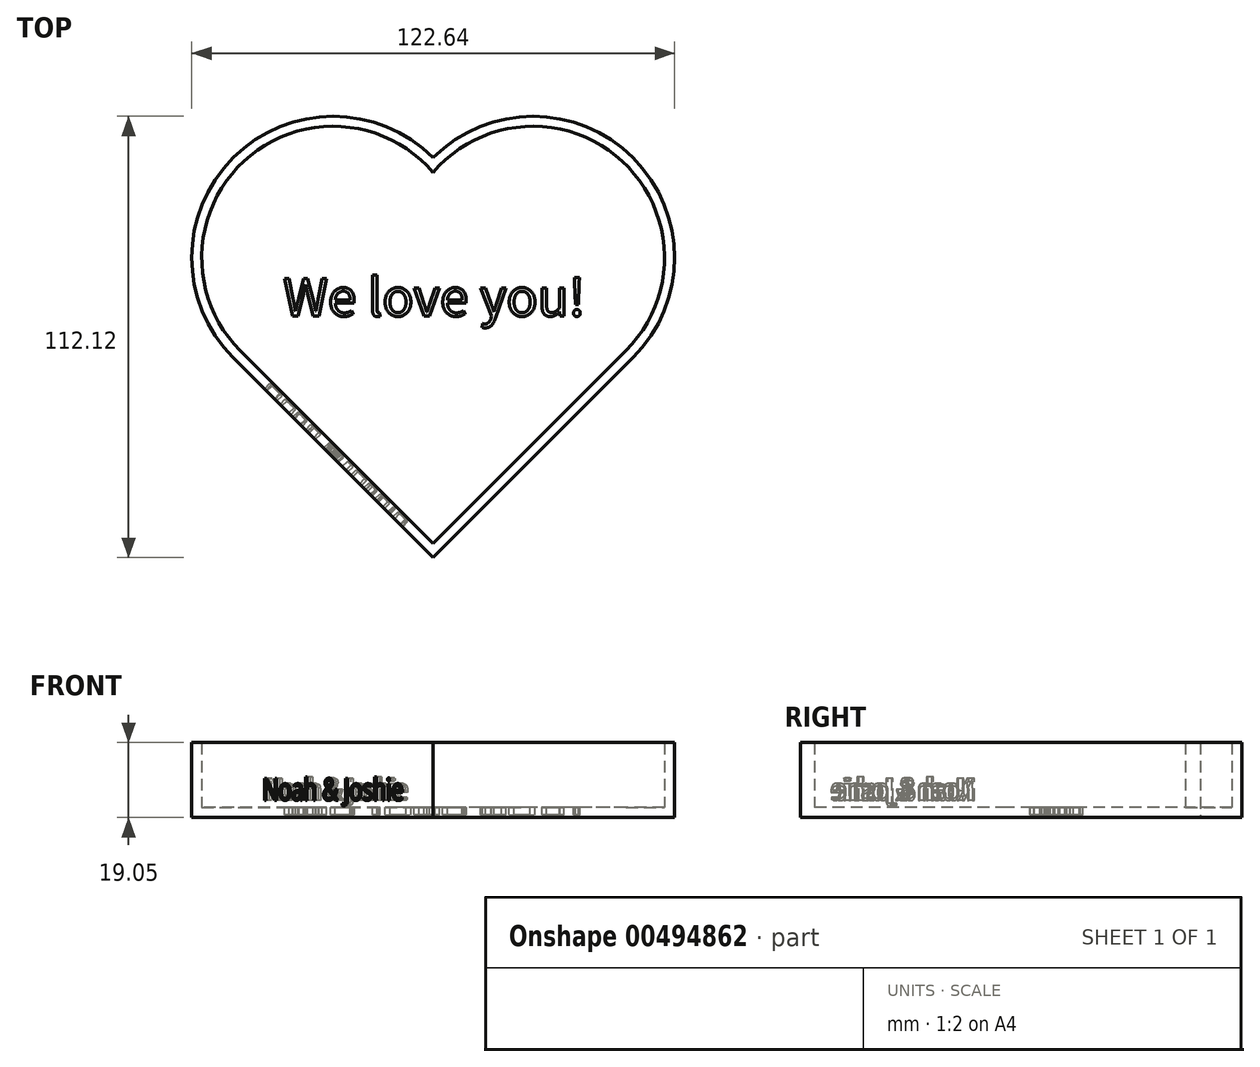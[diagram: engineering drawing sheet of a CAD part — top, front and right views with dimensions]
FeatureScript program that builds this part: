
annotation { "Feature Type Name" : "Feature", "Feature Type Description" : "" }
export const myFeature = defineFeature(function(context is Context, id is Id, definition is map)
    precondition{}
    {
        {
            var Q0;
            Q0=qCreatedBy(makeId("Top.planeOp"),FACE);
            var sketch = newSketch(context, id + "F0", { "sketchPlane" : qUnion([Q0])});
            skLineSegment(sketch, "E0", {"start": v(0, 50.8) * mm, "end": v(0, 0) * mm, "construction": true});
            skLineSegment(sketch, "E1", {"start": v(0, 0) * mm, "end": v(50.8, 0) * mm, "construction": true});
            skLineSegment(sketch, "E2", {"start": v(0, 0) * mm, "end": v(0, -50.8) * mm, "construction": true});
            skLineSegment(sketch, "E3", {"start": v(0, 0) * mm, "end": v(-50.8, 0) * mm, "construction": true});
            skLineSegment(sketch, "E4", {"start": v(-50.8, 0) * mm, "end": v(0, -50.8) * mm});
            skLineSegment(sketch, "E5", {"start": v(50.8, 0) * mm, "end": v(0, -50.8) * mm});
            skArc(sketch, "E6", {"start": v(0, 50.8) * mm, "mid": v(-50.8, 50.8) * mm, "end": v(-50.8, 0) * mm});
            skArc(sketch, "E7", {"start": v(50.8, 0) * mm, "mid": v(50.8, 50.8) * mm, "end": v(0, 50.8) * mm});
            skSolve(sketch);
        }
        {
            var Q0;
            Q0=makeQuery(id+"F0.imprint","IMPRINT",FACE,{"disambiguationData":[TD([[makeQuery(id+"F0.imprint","IMPRINT",EDGE,{"derivedFrom":sQuery(id+"F0.wireOp",EDGE,"E4")}),1.0]])]});
            extrude(context, id + "F1", {"entities" : qUnion([Q0]), "depth" : 19.05 * mm});
        }
        {
            var Q0;
            Q0=makeQuery(id+"F1.opExtrude","CAP_FACE",FACE,{"disambiguationData":[OSD([sQuery(id+"F0.wireOp",EDGE,"E4"),sQuery(id+"F0.wireOp",EDGE,"E5"),sQuery(id+"F0.wireOp",EDGE,"E6"),sQuery(id+"F0.wireOp",EDGE,"E7")])],"isStart":false});
            shell(context, id + "F2", {"entities" : qUnion([Q0]), "thickness" : 2.54 * mm});
        }
        {
            var Q0;
            Q0=makeQuery(id+"F2.opShell","OFFSET_FACE",FACE,{"disambiguationData":[OSD([sQuery(id+"F0.wireOp",EDGE,"E4"),sQuery(id+"F0.wireOp",EDGE,"E5"),sQuery(id+"F0.wireOp",EDGE,"E6"),sQuery(id+"F0.wireOp",EDGE,"E7")])]});
            var sketch = newSketch(context, id + "F3", { "sketchPlane" : qUnion([Q0])});
            skLineSegment(sketch, "E8.bottom", {"start": v(38.1, 19.96) * mm, "end": v(-38.1, 19.96) * mm, "construction": true});
            skLineSegment(sketch, "E8.top", {"start": v(38.1, 10.6) * mm, "end": v(-38.1, 10.6) * mm, "construction": true});
            skLineSegment(sketch, "E8.left", {"start": v(38.1, 19.96) * mm, "end": v(38.1, 10.6) * mm, "construction": true});
            skLineSegment(sketch, "E8.right", {"start": v(-38.1, 19.96) * mm, "end": v(-38.1, 10.6) * mm, "construction": true});
            skPoint(sketch, "E8.middle", {"position": v(0, 15.28) * mm});
            skText(sketch, "E9", { "text": "We love you!", "fontName": "NotoSansCJKkr-Regular.otf"});
            const initialGuessF3  = {"E9": [-0.0381, 0.0106, 1, 0, 0.00936]};
            skSetInitialGuess(sketch, initialGuessF3);
            skSolve(sketch);
        }
        {
            var Q0;
            Q0 = qSketchRegion(id + "F3", true);
            extrude(context, id + "F4", {"entities" : qUnion([Q0]), "operationType" : NewBodyOperationType.REMOVE, "oppositeDirection" : true, "depth" : 1.9 * mm});
        }
        {
            var Q0;
            Q0=makeQuery(id+"F1.opExtrude","SWEPT_FACE",FACE,{"disambiguationData":[OSD([sQuery(id+"F0.wireOp",EDGE,"E4")])]});
            var sketch = newSketch(context, id + "F5", { "sketchPlane" : qUnion([Q0])});
            skText(sketch, "E10", { "text": "Noah & Joshie", "fontName": "OpenSans-Regular.ttf"});
            skLineSegment(sketch, "E11", {"start": v(-35.92, 0) * mm, "end": v(35.92, 0) * mm, "construction": true});
            skLineSegment(sketch, "E12", {"start": v(-25.4, 4.42) * mm, "end": v(-35.92, 4.42) * mm, "construction": true});
            const initialGuessF5  = {"E10": [-0.0254, 0.00442, 1, 0, 0.00557]};
            skSetInitialGuess(sketch, initialGuessF5);
            skSolve(sketch);
        }
        {
            var Q0;
            Q0 = qSketchRegion(id + "F5", true);
            extrude(context, id + "F6", {"entities" : qUnion([Q0]), "operationType" : NewBodyOperationType.REMOVE, "oppositeDirection" : true, "depth" : 1.9 * mm});
        }
    });
